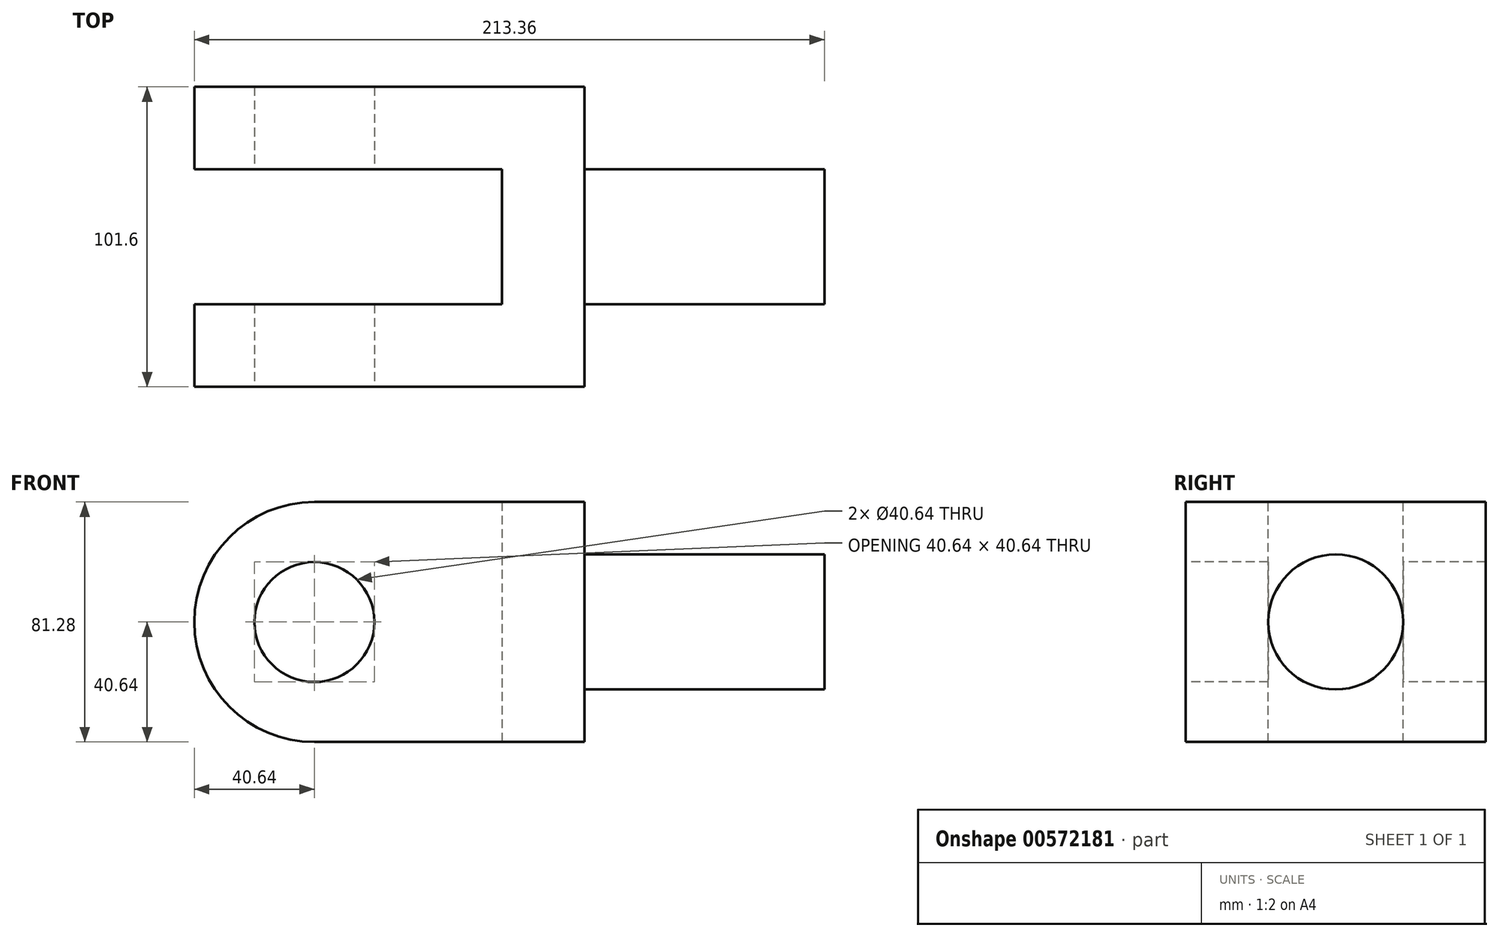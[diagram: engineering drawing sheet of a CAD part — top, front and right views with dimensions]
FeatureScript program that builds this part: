
annotation { "Feature Type Name" : "Feature", "Feature Type Description" : "" }
export const myFeature = defineFeature(function(context is Context, id is Id, definition is map)
    precondition{}
    {
        {
            var Q0;
            Q0=qCreatedBy(makeId("Top.planeOp"),FACE);
            var sketch = newSketch(context, id + "F0", { "sketchPlane" : qUnion([Q0])});
            skLineSegment(sketch, "E0", {"start": v(0, 0) * mm, "end": v(0, 36.95) * mm});
            skLineSegment(sketch, "E1", {"start": v(0, 36.95) * mm, "end": v(0, -64.65) * mm});
            skLineSegment(sketch, "E2", {"start": v(0, 36.95) * mm, "end": v(-132.08, 36.95) * mm});
            skLineSegment(sketch, "E3", {"start": v(-132.08, 36.95) * mm, "end": v(-132.08, 9) * mm});
            skLineSegment(sketch, "E4", {"start": v(-132.08, 9) * mm, "end": v(-27.94, 9) * mm});
            skLineSegment(sketch, "E5", {"start": v(-27.94, 9) * mm, "end": v(-27.94, -36.71) * mm});
            skLineSegment(sketch, "E6", {"start": v(0, -64.65) * mm, "end": v(-132.08, -64.65) * mm});
            skLineSegment(sketch, "E7", {"start": v(-132.08, -64.65) * mm, "end": v(-132.08, -36.71) * mm});
            skLineSegment(sketch, "E8", {"start": v(-132.08, -36.71) * mm, "end": v(-27.94, -36.71) * mm});
            skLineSegment(sketch, "E9", {"start": v(0, 9) * mm, "end": v(81.28, 9) * mm});
            skLineSegment(sketch, "E10", {"start": v(81.28, 9) * mm, "end": v(81.28, -36.71) * mm});
            skLineSegment(sketch, "E11", {"start": v(81.28, -36.71) * mm, "end": v(0, -36.71) * mm});
            skSolve(sketch);
        }
        {
            var Q0;
            {var subQ1=sQuery(id+"F0.wireOp",EDGE,"E2");Q0=makeQuery(id+"F0.imprint","IMPRINT",FACE,{"disambiguationData":[TD([[makeQuery(id+"F0.imprint","IMPRINT",EDGE,{"derivedFrom":subQ1}),1.0]])]});}
            extrude(context, id + "F1", {"entities" : qUnion([Q0]), "depth" : 81.28 * mm, "offsetDistance" : 25.4 * mm});
        }
        {
            var Q0;
            Q0=makeQuery(id+"F1.opExtrude","SWEPT_FACE",FACE,{"disambiguationData":[OSD([sQuery(id+"F0.wireOp",EDGE,"E6")])]});
            var sketch = newSketch(context, id + "F2", { "sketchPlane" : qUnion([Q0])});
            skLineSegment(sketch, "E12", {"start": v(0, 0) * mm, "end": v(-91.44, 0) * mm});
            skCircle(sketch, "E13", {"center": v(-91.44, 40.64) * mm, "radius": 20.32 * mm});
            skSolve(sketch);
        }
        {
            var Q0;
            Q0=makeQuery(id+"F2.imprint","IMPRINT",FACE,{"disambiguationData":[TD([[makeQuery(id+"F2.imprint","IMPRINT",EDGE,{"derivedFrom":sQuery(id+"F2.wireOp",EDGE,"E13")}),1.0]])]});
            extrude(context, id + "F3", {"entities" : qUnion([Q0]), "operationType" : NewBodyOperationType.REMOVE, "oppositeDirection" : true, "depth" : 101.6 * mm, "offsetDistance" : 25.4 * mm});
        }
        {
            var Q0;
            Q0=makeQuery(id+"F1.opExtrude","CAP_EDGE",EDGE,{"disambiguationData":[OSD([sQuery(id+"F0.wireOp",EDGE,"E7")])],"isStart":false});
            var Q1;
            Q1=makeQuery(id+"F1.opExtrude","CAP_EDGE",EDGE,{"disambiguationData":[OSD([sQuery(id+"F0.wireOp",EDGE,"E7")])],"isStart":true});
            fillet(context, id + "F4", {"entities" : qUnion([Q0, Q1]), "radius" : 40.64 * mm, "tangentPropagation" : true, "allowEdgeOverflow" : false});
        }
        {
            var Q0;
            Q0=makeQuery(id+"F1.opExtrude","CAP_EDGE",EDGE,{"disambiguationData":[OSD([sQuery(id+"F0.wireOp",EDGE,"E3")])],"isStart":false});
            var Q1;
            Q1=makeQuery(id+"F1.opExtrude","CAP_EDGE",EDGE,{"disambiguationData":[OSD([sQuery(id+"F0.wireOp",EDGE,"E3")])],"isStart":true});
            fillet(context, id + "F5", {"entities" : qUnion([Q0, Q1]), "radius" : 40.64 * mm, "tangentPropagation" : true, "allowEdgeOverflow" : false});
        }
        {
            var Q0;
            Q0=makeQuery(id+"F1.opExtrude","SWEPT_FACE",FACE,{"disambiguationData":[OSD([sQuery(id+"F0.wireOp",EDGE,"E1")])]});
            var sketch = newSketch(context, id + "F6", { "sketchPlane" : qUnion([Q0])});
            skCircle(sketch, "E14", {"center": v(-13.85, 40.64) * mm, "radius": 22.86 * mm});
            skSolve(sketch);
        }
        {
            var Q0;
            Q0=makeQuery(id+"F6.imprint","IMPRINT",FACE,{"disambiguationData":[TD([[makeQuery(id+"F6.imprint","IMPRINT",EDGE,{"derivedFrom":sQuery(id+"F6.wireOp",EDGE,"E14")}),1.0]])]});
            extrude(context, id + "F7", {"entities" : qUnion([Q0]), "operationType" : NewBodyOperationType.ADD, "depth" : 81.28 * mm, "offsetDistance" : 25.4 * mm});
        }
    });
